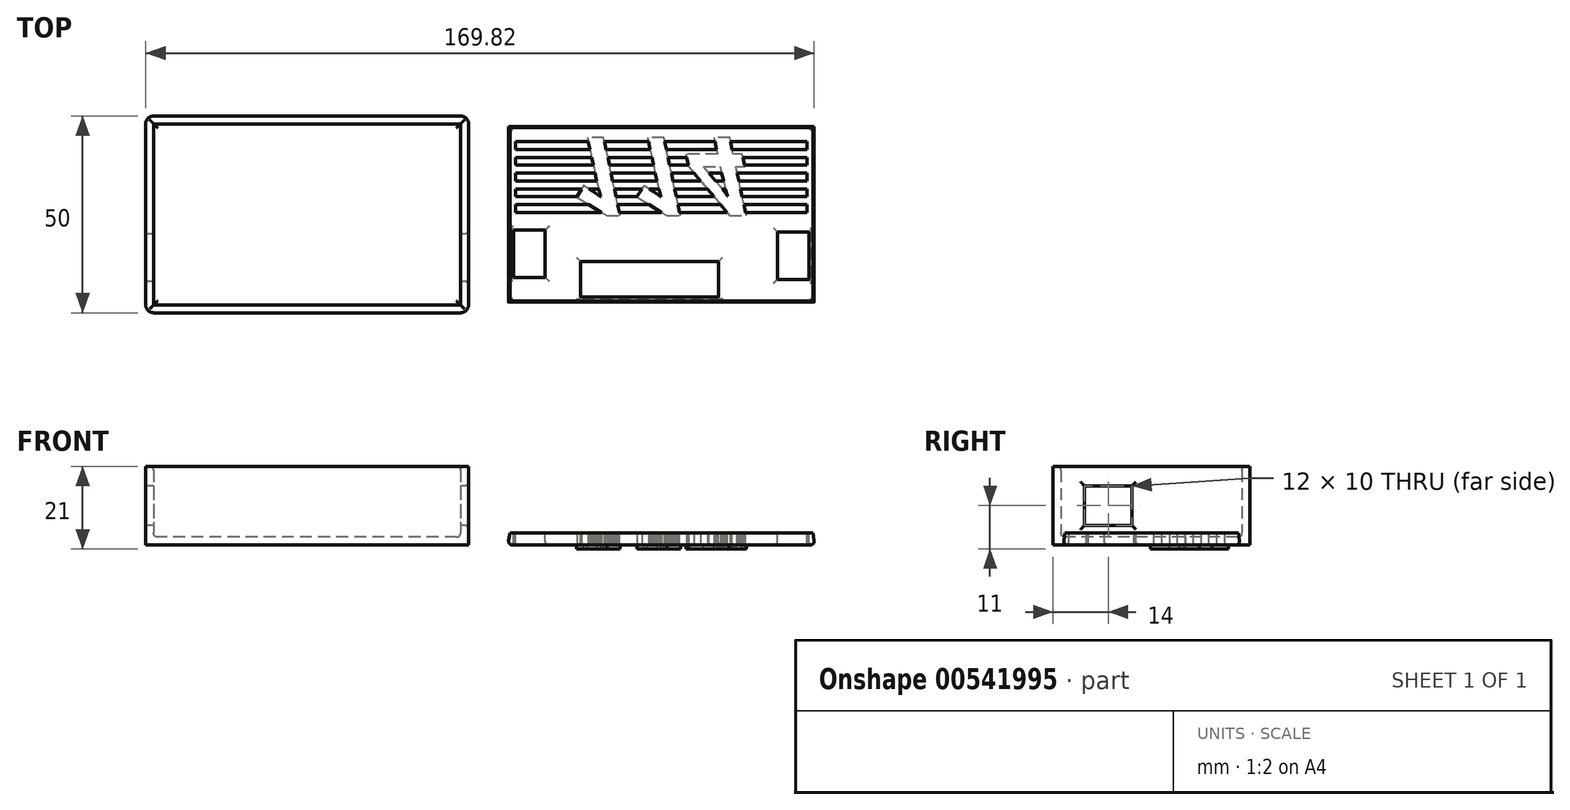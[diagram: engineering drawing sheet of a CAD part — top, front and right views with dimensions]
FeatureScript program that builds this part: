
annotation { "Feature Type Name" : "Feature", "Feature Type Description" : "" }
export const myFeature = defineFeature(function(context is Context, id is Id, definition is map)
    precondition{}
    {
        {
            var Q0;
            Q0=qCreatedBy(makeId("Top.planeOp"),FACE);
            var sketch = newSketch(context, id + "F0", { "sketchPlane" : qUnion([Q0])});
            skLineSegment(sketch, "E0.bottom", {"start": v(41, 25) * mm, "end": v(-41, 25) * mm});
            skLineSegment(sketch, "E0.top", {"start": v(41, -25) * mm, "end": v(-41, -25) * mm});
            skLineSegment(sketch, "E0.left", {"start": v(41, 25) * mm, "end": v(41, -25) * mm});
            skLineSegment(sketch, "E0.right", {"start": v(-41, 25) * mm, "end": v(-41, -25) * mm});
            skPoint(sketch, "E0.middle", {"position": v(0, 0) * mm});
            skSolve(sketch);
        }
        {
            var Q0;
            Q0 = qSketchRegion(id + "F0", true);
            extrude(context, id + "F1", {"entities" : qUnion([Q0]), "depth" : 20 * mm, "offsetDistance" : 25 * mm});
        }
        {
            var Q0;
            Q0=makeQuery(id+"F1.opExtrude","CAP_FACE",FACE,{"disambiguationData":[OSD([sQuery(id+"F0.wireOp",EDGE,"E0.bottom"),sQuery(id+"F0.wireOp",EDGE,"E0.top"),sQuery(id+"F0.wireOp",EDGE,"E0.left"),sQuery(id+"F0.wireOp",EDGE,"E0.right")])],"isStart":false});
            shell(context, id + "F2", {"entities" : qUnion([Q0]), "thickness" : 2 * mm});
        }
        {
            var Q0;
            Q0=makeQuery(id+"F1.opExtrude","SWEPT_EDGE",EDGE,{"disambiguationData":[OSD([sQuery(id+"F0.wireOp",EDGE,"E0.top"),sQuery(id+"F0.wireOp",EDGE,"E0.left")])]});
            var Q1;
            Q1=makeQuery(id+"F1.opExtrude","SWEPT_EDGE",EDGE,{"disambiguationData":[OSD([sQuery(id+"F0.wireOp",EDGE,"E0.top"),sQuery(id+"F0.wireOp",EDGE,"E0.right")])]});
            var Q2;
            Q2=makeQuery(id+"F1.opExtrude","SWEPT_EDGE",EDGE,{"disambiguationData":[OSD([sQuery(id+"F0.wireOp",EDGE,"E0.bottom"),sQuery(id+"F0.wireOp",EDGE,"E0.left")])]});
            var Q3;
            Q3=makeQuery(id+"F1.opExtrude","SWEPT_EDGE",EDGE,{"disambiguationData":[OSD([sQuery(id+"F0.wireOp",EDGE,"E0.bottom"),sQuery(id+"F0.wireOp",EDGE,"E0.right")])]});
            fillet(context, id + "F3", {"entities" : qUnion([Q0, Q1, Q2, Q3]), "radius" : 2 * mm, "tangentPropagation" : true, "allowEdgeOverflow" : false});
        }
        {
            var Q0;
            {var subQ0=sQuery(id+"F0.wireOp",EDGE,"E0.right");Q0=makeQuery(id+"F2.opShell","OFFSET_EDGE",EDGE,{"disambiguationData":[OSD([subQ0]),TDD([makeQuery(id+"F1.opExtrude","CAP_EDGE",EDGE,{"disambiguationData":[OSD([subQ0])],"isStart":false})])]});}
            var Q1;
            {var subQ0=sQuery(id+"F0.wireOp",EDGE,"E0.top");Q1=makeQuery(id+"F2.opShell","OFFSET_EDGE",EDGE,{"disambiguationData":[OSD([subQ0]),TDD([makeQuery(id+"F1.opExtrude","CAP_EDGE",EDGE,{"disambiguationData":[OSD([subQ0])],"isStart":false})])]});}
            var Q2;
            {var subQ0=sQuery(id+"F0.wireOp",EDGE,"E0.left");Q2=makeQuery(id+"F2.opShell","OFFSET_EDGE",EDGE,{"disambiguationData":[OSD([subQ0]),TDD([makeQuery(id+"F1.opExtrude","CAP_EDGE",EDGE,{"disambiguationData":[OSD([subQ0])],"isStart":false})])]});}
            var Q3;
            {var subQ0=sQuery(id+"F0.wireOp",EDGE,"E0.bottom");Q3=makeQuery(id+"F2.opShell","OFFSET_EDGE",EDGE,{"disambiguationData":[OSD([subQ0]),TDD([makeQuery(id+"F1.opExtrude","CAP_EDGE",EDGE,{"disambiguationData":[OSD([subQ0])],"isStart":true})])]});}
            var Q4;
            {var subQ0=sQuery(id+"F0.wireOp",EDGE,"E0.top");Q4=makeQuery(id+"F2.opShell","OFFSET_EDGE",EDGE,{"disambiguationData":[OSD([subQ0]),TDD([makeQuery(id+"F1.opExtrude","CAP_EDGE",EDGE,{"disambiguationData":[OSD([subQ0])],"isStart":true})])]});}
            var Q5;
            {var subQ0=sQuery(id+"F0.wireOp",EDGE,"E0.right");Q5=makeQuery(id+"F2.opShell","OFFSET_EDGE",EDGE,{"disambiguationData":[OSD([subQ0]),TDD([makeQuery(id+"F1.opExtrude","CAP_EDGE",EDGE,{"disambiguationData":[OSD([subQ0])],"isStart":true})])]});}
            var Q6;
            {var subQ0=sQuery(id+"F0.wireOp",EDGE,"E0.left");Q6=makeQuery(id+"F2.opShell","OFFSET_EDGE",EDGE,{"disambiguationData":[OSD([subQ0]),TDD([makeQuery(id+"F1.opExtrude","CAP_EDGE",EDGE,{"disambiguationData":[OSD([subQ0])],"isStart":true})])]});}
            var Q7;
            {var subQ0=sQuery(id+"F0.wireOp",EDGE,"E0.bottom");Q7=makeQuery(id+"F2.opShell","OFFSET_EDGE",EDGE,{"disambiguationData":[OSD([subQ0]),TDD([makeQuery(id+"F1.opExtrude","CAP_EDGE",EDGE,{"disambiguationData":[OSD([subQ0])],"isStart":false})])]});}
            fillet(context, id + "F4", {"entities" : qUnion([Q0, Q1, Q2, Q3, Q4, Q5, Q6, Q7]), "radius" : 1 * mm, "tangentPropagation" : true, "allowEdgeOverflow" : false});
        }
        {
            var Q0;
            Q0=qCreatedBy(makeId("Top.planeOp"),FACE);
            var sketch = newSketch(context, id + "F5", { "sketchPlane" : qUnion([Q0])});
            skLineSegment(sketch, "E1.bottom", {"start": v(129, 22.5) * mm, "end": v(51, 22.5) * mm});
            skLineSegment(sketch, "E1.top", {"start": v(129, -22.5) * mm, "end": v(51, -22.5) * mm});
            skLineSegment(sketch, "E1.left", {"start": v(129, 22.5) * mm, "end": v(129, -22.5) * mm});
            skLineSegment(sketch, "E1.right", {"start": v(51, 22.5) * mm, "end": v(51, -22.5) * mm});
            skPoint(sketch, "E1.middle", {"position": v(90, 0) * mm});
            skSolve(sketch);
        }
        {
            var Q0;
            Q0 = qSketchRegion(id + "F5", true);
            extrude(context, id + "F6", {"entities" : qUnion([Q0]), "depth" : 3 * mm, "offsetDistance" : 25 * mm});
        }
        {
            var Q0;
            Q0=makeQuery(id+"F6.opExtrude","CAP_FACE",FACE,{"disambiguationData":[OSD([sQuery(id+"F5.wireOp",EDGE,"E1.bottom"),sQuery(id+"F5.wireOp",EDGE,"E1.top"),sQuery(id+"F5.wireOp",EDGE,"E1.left"),sQuery(id+"F5.wireOp",EDGE,"E1.right")])],"isStart":false});
            shell(context, id + "F7", {"entities" : qUnion([Q0]), "thickness" : 2 * mm});
        }
        {
            var Q0;
            Q0=makeQuery(id+"F6.opExtrude","CAP_EDGE",EDGE,{"disambiguationData":[OSD([sQuery(id+"F5.wireOp",EDGE,"E1.top")])],"isStart":false});
            var Q1;
            Q1=makeQuery(id+"F6.opExtrude","CAP_EDGE",EDGE,{"disambiguationData":[OSD([sQuery(id+"F5.wireOp",EDGE,"E1.left")])],"isStart":false});
            var Q2;
            Q2=makeQuery(id+"F6.opExtrude","CAP_EDGE",EDGE,{"disambiguationData":[OSD([sQuery(id+"F5.wireOp",EDGE,"E1.bottom")])],"isStart":false});
            var Q3;
            Q3=makeQuery(id+"F6.opExtrude","CAP_EDGE",EDGE,{"disambiguationData":[OSD([sQuery(id+"F5.wireOp",EDGE,"E1.right")])],"isStart":false});
            chamfer(context, id + "F8", {"entities" : qUnion([Q0, Q1, Q2, Q3]), "chamferType" : ChamferType.TWO_OFFSETS, "width1" : 3 * mm, "oppositeDirection" : false, "width2" : .5 * mm, "tangentPropagation" : true});
        }
        {
            var Q0;
            Q0=makeQuery(id+"F7.opShell","OFFSET_FACE",FACE,{"disambiguationData":[OSD([sQuery(id+"F5.wireOp",EDGE,"E1.bottom"),sQuery(id+"F5.wireOp",EDGE,"E1.top"),sQuery(id+"F5.wireOp",EDGE,"E1.left"),sQuery(id+"F5.wireOp",EDGE,"E1.right")])]});
            var sketch = newSketch(context, id + "F9", { "sketchPlane" : qUnion([Q0])});
            skLineSegment(sketch, "E2.bottom", {"start": v(52.5, -16) * mm, "end": v(60.5, -16) * mm});
            skLineSegment(sketch, "E2.top", {"start": v(52.5, -4) * mm, "end": v(60.5, -4) * mm});
            skLineSegment(sketch, "E2.left", {"start": v(52.5, -16) * mm, "end": v(52.5, -4) * mm});
            skLineSegment(sketch, "E2.right", {"start": v(60.5, -16) * mm, "end": v(60.5, -4) * mm});
            skLineSegment(sketch, "E3.bottom", {"start": v(119.5, -16.5) * mm, "end": v(127.5, -16.5) * mm});
            skLineSegment(sketch, "E3.top", {"start": v(119.5, -4.5) * mm, "end": v(127.5, -4.5) * mm});
            skLineSegment(sketch, "E3.left", {"start": v(119.5, -16.5) * mm, "end": v(119.5, -4.5) * mm});
            skLineSegment(sketch, "E3.right", {"start": v(127.5, -16.5) * mm, "end": v(127.5, -4.5) * mm});
            skSolve(sketch);
        }
        {
            var Q0;
            Q0 = qSketchRegion(id + "F9", true);
            extrude(context, id + "F10", {"entities" : qUnion([Q0]), "operationType" : NewBodyOperationType.REMOVE, "oppositeDirection" : true, "depth" : 25 * mm, "offsetDistance" : 25 * mm, "symmetric" : true});
        }
        {
            var Q0;
            Q0=makeQuery(id+"F1.opExtrude","SWEPT_FACE",FACE,{"disambiguationData":[OSD([sQuery(id+"F0.wireOp",EDGE,"E0.right")])]});
            var sketch = newSketch(context, id + "F11", { "sketchPlane" : qUnion([Q0])});
            skLineSegment(sketch, "E4.bottom", {"start": v(5, 5) * mm, "end": v(17, 5) * mm});
            skLineSegment(sketch, "E4.top", {"start": v(5, 15) * mm, "end": v(17, 15) * mm});
            skLineSegment(sketch, "E4.left", {"start": v(5, 5) * mm, "end": v(5, 15) * mm});
            skLineSegment(sketch, "E4.right", {"start": v(17, 5) * mm, "end": v(17, 15) * mm});
            skSolve(sketch);
        }
        {
            var Q0;
            Q0 = qSketchRegion(id + "F11", true);
            extrude(context, id + "F12", {"entities" : qUnion([Q0]), "operationType" : NewBodyOperationType.REMOVE, "oppositeDirection" : true, "depth" : 90 * mm, "offsetDistance" : 25 * mm});
        }
        {
            var Q0;
            Q0=makeQuery(id+"F12.boolean.opBoolean","COPY",EDGE,{"derivedFrom":makeQuery(id+"F12.opExtrude","CAP_EDGE",EDGE,{"disambiguationData":[OSD([sQuery(id+"F11.wireOp",EDGE,"E4.left")])],"isStart":true})});
            var Q1;
            Q1=makeQuery(id+"F12.boolean.opBoolean","COPY",EDGE,{"derivedFrom":makeQuery(id+"F12.opExtrude","CAP_EDGE",EDGE,{"disambiguationData":[OSD([sQuery(id+"F11.wireOp",EDGE,"E4.top")])],"isStart":true})});
            var Q2;
            Q2=makeQuery(id+"F12.boolean.opBoolean","COPY",EDGE,{"derivedFrom":makeQuery(id+"F12.opExtrude","CAP_EDGE",EDGE,{"disambiguationData":[OSD([sQuery(id+"F11.wireOp",EDGE,"E4.right")])],"isStart":true})});
            var Q3;
            Q3=makeQuery(id+"F12.boolean.opBoolean","COPY",EDGE,{"derivedFrom":makeQuery(id+"F12.opExtrude","CAP_EDGE",EDGE,{"disambiguationData":[OSD([sQuery(id+"F11.wireOp",EDGE,"E4.bottom")])],"isStart":true})});
            var Q4;
            Q4=makeQuery(id+"F12.boolean.opBoolean","INTERSECT",EDGE,{"derivedFrom":[makeQuery(id+"F1.opExtrude","SWEPT_FACE",FACE,{"disambiguationData":[OSD([sQuery(id+"F0.wireOp",EDGE,"E0.left")])]}),makeQuery(id+"F12.opExtrude","SWEPT_FACE",FACE,{"disambiguationData":[OSD([sQuery(id+"F11.wireOp",EDGE,"E4.right")])]})]});
            var Q5;
            Q5=makeQuery(id+"F12.boolean.opBoolean","INTERSECT",EDGE,{"derivedFrom":[makeQuery(id+"F1.opExtrude","SWEPT_FACE",FACE,{"disambiguationData":[OSD([sQuery(id+"F0.wireOp",EDGE,"E0.left")])]}),makeQuery(id+"F12.opExtrude","SWEPT_FACE",FACE,{"disambiguationData":[OSD([sQuery(id+"F11.wireOp",EDGE,"E4.top")])]})]});
            var Q6;
            Q6=makeQuery(id+"F12.boolean.opBoolean","INTERSECT",EDGE,{"derivedFrom":[makeQuery(id+"F1.opExtrude","SWEPT_FACE",FACE,{"disambiguationData":[OSD([sQuery(id+"F0.wireOp",EDGE,"E0.left")])]}),makeQuery(id+"F12.opExtrude","SWEPT_FACE",FACE,{"disambiguationData":[OSD([sQuery(id+"F11.wireOp",EDGE,"E4.left")])]})]});
            var Q7;
            Q7=makeQuery(id+"F12.boolean.opBoolean","INTERSECT",EDGE,{"derivedFrom":[makeQuery(id+"F1.opExtrude","SWEPT_FACE",FACE,{"disambiguationData":[OSD([sQuery(id+"F0.wireOp",EDGE,"E0.left")])]}),makeQuery(id+"F12.opExtrude","SWEPT_FACE",FACE,{"disambiguationData":[OSD([sQuery(id+"F11.wireOp",EDGE,"E4.bottom")])]})]});
            fillet(context, id + "F13", {"entities" : qUnion([Q0, Q1, Q2, Q3, Q4, Q5, Q6, Q7]), "radius" : 1 * mm, "tangentPropagation" : true, "allowEdgeOverflow" : false});
        }
        {
            var Q0;
            Q0=makeQuery(id+"F7.opShell","OFFSET_FACE",FACE,{"disambiguationData":[OSD([sQuery(id+"F5.wireOp",EDGE,"E1.bottom"),sQuery(id+"F5.wireOp",EDGE,"E1.top"),sQuery(id+"F5.wireOp",EDGE,"E1.left"),sQuery(id+"F5.wireOp",EDGE,"E1.right")])]});
            var sketch = newSketch(context, id + "F14", { "sketchPlane" : qUnion([Q0])});
            skLineSegment(sketch, "E5.bottom", {"start": v(69.5, -21) * mm, "end": v(104.5, -21) * mm});
            skLineSegment(sketch, "E5.top", {"start": v(69.5, -12) * mm, "end": v(104.5, -12) * mm});
            skLineSegment(sketch, "E5.left", {"start": v(69.5, -21) * mm, "end": v(69.5, -12) * mm});
            skLineSegment(sketch, "E5.right", {"start": v(104.5, -21) * mm, "end": v(104.5, -12) * mm});
            skSolve(sketch);
        }
        {
            var Q0;
            Q0 = qSketchRegion(id + "F14", true);
            extrude(context, id + "F15", {"entities" : qUnion([Q0]), "operationType" : NewBodyOperationType.REMOVE, "oppositeDirection" : true, "depth" : 25 * mm, "offsetDistance" : 25 * mm, "symmetric" : true});
        }
        {
            var Q0;
            Q0=makeQuery(id+"F7.opShell","OFFSET_FACE",FACE,{"disambiguationData":[OSD([sQuery(id+"F5.wireOp",EDGE,"E1.bottom"),sQuery(id+"F5.wireOp",EDGE,"E1.top"),sQuery(id+"F5.wireOp",EDGE,"E1.left"),sQuery(id+"F5.wireOp",EDGE,"E1.right")])]});
            var sketch = newSketch(context, id + "F16", { "sketchPlane" : qUnion([Q0])});
            skLineSegment(sketch, "E6.bottom", {"start": v(53, 16.5) * mm, "end": v(127, 16.5) * mm});
            skLineSegment(sketch, "E6.top", {"start": v(53, 18.5) * mm, "end": v(127, 18.5) * mm});
            skLineSegment(sketch, "E6.left", {"start": v(53, 16.5) * mm, "end": v(53, 18.5) * mm});
            skLineSegment(sketch, "E6.right", {"start": v(127, 16.5) * mm, "end": v(127, 18.5) * mm});
            skLineSegment(sketch, "E7.bottom", {"start": v(53, 12.5) * mm, "end": v(127, 12.5) * mm});
            skLineSegment(sketch, "E7.top", {"start": v(53, 14.5) * mm, "end": v(127, 14.5) * mm});
            skLineSegment(sketch, "E7.left", {"start": v(53, 12.5) * mm, "end": v(53, 14.5) * mm});
            skLineSegment(sketch, "E7.right", {"start": v(127, 12.5) * mm, "end": v(127, 14.5) * mm});
            skLineSegment(sketch, "E8.bottom", {"start": v(53, 8.5) * mm, "end": v(127, 8.5) * mm});
            skLineSegment(sketch, "E8.top", {"start": v(53, 10.5) * mm, "end": v(127, 10.5) * mm});
            skLineSegment(sketch, "E8.left", {"start": v(53, 8.5) * mm, "end": v(53, 10.5) * mm});
            skLineSegment(sketch, "E8.right", {"start": v(127, 8.5) * mm, "end": v(127, 10.5) * mm});
            skLineSegment(sketch, "E9.bottom", {"start": v(53, 4.5) * mm, "end": v(127, 4.5) * mm});
            skLineSegment(sketch, "E9.top", {"start": v(53, 6.5) * mm, "end": v(127, 6.5) * mm});
            skLineSegment(sketch, "E9.left", {"start": v(53, 4.5) * mm, "end": v(53, 6.5) * mm});
            skLineSegment(sketch, "E9.right", {"start": v(127, 4.5) * mm, "end": v(127, 6.5) * mm});
            skLineSegment(sketch, "E10.bottom", {"start": v(53, 0.5) * mm, "end": v(127, 0.5) * mm});
            skLineSegment(sketch, "E10.top", {"start": v(53, 2.5) * mm, "end": v(127, 2.5) * mm});
            skLineSegment(sketch, "E10.left", {"start": v(53, 0.5) * mm, "end": v(53, 2.5) * mm});
            skLineSegment(sketch, "E10.right", {"start": v(127, 0.5) * mm, "end": v(127, 2.5) * mm});
            skSolve(sketch);
        }
        {
            var Q0;
            Q0 = qSketchRegion(id + "F16", true);
            extrude(context, id + "F17", {"entities" : qUnion([Q0]), "operationType" : NewBodyOperationType.REMOVE, "oppositeDirection" : true, "depth" : 25 * mm, "offsetDistance" : 25 * mm});
        }
        {
            var Q0;
            Q0=makeQuery(id+"F6.opExtrude","CAP_FACE",FACE,{"disambiguationData":[OSD([sQuery(id+"F5.wireOp",EDGE,"E1.bottom"),sQuery(id+"F5.wireOp",EDGE,"E1.top"),sQuery(id+"F5.wireOp",EDGE,"E1.left"),sQuery(id+"F5.wireOp",EDGE,"E1.right")])],"isStart":true});
            var sketch = newSketch(context, id + "F18", { "sketchPlane" : qUnion([Q0])});
            skText(sketch, "E11", { "text": "114", "fontName": "OpenSans-BoldItalic.ttf"});
            const initialGuessF18  = {"E11": [0.066, -0.0195, 1, 0, 0.02]};
            skSetInitialGuess(sketch, initialGuessF18);
            skSolve(sketch);
        }
        {
            var Q0;
            Q0 = qSketchRegion(id + "F18", true);
            extrude(context, id + "F19", {"entities" : qUnion([Q0]), "operationType" : NewBodyOperationType.ADD, "depth" : 4 * mm, "offsetDistance" : 25 * mm, "symmetric" : true});
        }
        {
            var Q0;
            {var subQ4=sQuery(id+"F5.wireOp",EDGE,"E1.left");var subQ9=sQuery(id+"F5.wireOp",EDGE,"E1.right");var subQ14=sQuery(id+"F5.wireOp",EDGE,"E1.top");var subQ15=sQuery(id+"F5.wireOp",EDGE,"E1.bottom");var subQ16=makeQuery(id+"F7.opShell","OFFSET_FACE",FACE,{"disambiguationData":[OSD([subQ15,subQ14,subQ4,subQ9])]});Q0=makeQuery(id+"F19.boolean.opBoolean","MERGE",FACE,{"derivedFrom":[makeQuery(id+"F17.boolean.opBoolean","SPLIT",FACE,{"disambiguationData":[TD([makeQuery(id+"F7.opShell","OFFSET_FACE",FACE,{"disambiguationData":[OSD([subQ15])]})])],"derivedFrom":subQ16}),makeQuery(id+"F17.boolean.opBoolean","SPLIT",FACE,{"disambiguationData":[TD([makeQuery(id+"F7.opShell","OFFSET_FACE",FACE,{"disambiguationData":[OSD([subQ14])]})])],"derivedFrom":subQ16}),makeQuery(id+"F17.boolean.opBoolean","SPLIT",FACE,{"disambiguationData":[TD([makeQuery(id+"F17.opExtrude","SWEPT_FACE",FACE,{"disambiguationData":[OSD([sQuery(id+"F16.wireOp",EDGE,"E6.bottom")])]})])],"derivedFrom":subQ16}),makeQuery(id+"F17.boolean.opBoolean","SPLIT",FACE,{"disambiguationData":[TD([makeQuery(id+"F17.opExtrude","SWEPT_FACE",FACE,{"disambiguationData":[OSD([sQuery(id+"F16.wireOp",EDGE,"E7.bottom")])]})])],"derivedFrom":subQ16}),makeQuery(id+"F17.boolean.opBoolean","SPLIT",FACE,{"disambiguationData":[TD([makeQuery(id+"F17.opExtrude","SWEPT_FACE",FACE,{"disambiguationData":[OSD([sQuery(id+"F16.wireOp",EDGE,"E8.bottom")])]})])],"derivedFrom":subQ16}),makeQuery(id+"F17.boolean.opBoolean","SPLIT",FACE,{"disambiguationData":[TD([makeQuery(id+"F17.opExtrude","SWEPT_FACE",FACE,{"disambiguationData":[OSD([sQuery(id+"F16.wireOp",EDGE,"E9.bottom")])]})])],"derivedFrom":subQ16}),makeQuery(id+"F19.opExtrude","CAP_FACE",FACE,{"disambiguationData":[OSD([sQuery(id+"F18.wireOp",EDGE,"E11.sketch_text.stroke-0"),sQuery(id+"F18.wireOp",EDGE,"E11.sketch_text.stroke-1"),sQuery(id+"F18.wireOp",EDGE,"E11.sketch_text.stroke-2"),sQuery(id+"F18.wireOp",EDGE,"E11.sketch_text.stroke-3"),sQuery(id+"F18.wireOp",EDGE,"E11.sketch_text.stroke-4"),sQuery(id+"F18.wireOp",EDGE,"E11.sketch_text.stroke-5"),sQuery(id+"F18.wireOp",EDGE,"E11.sketch_text.stroke-6"),sQuery(id+"F18.wireOp",EDGE,"E11.sketch_text.stroke-7"),sQuery(id+"F18.wireOp",EDGE,"E11.sketch_text.stroke-8")])],"isStart":true}),makeQuery(id+"F19.opExtrude","CAP_FACE",FACE,{"disambiguationData":[OSD([sQuery(id+"F18.wireOp",EDGE,"E11.sketch_text.stroke-9"),sQuery(id+"F18.wireOp",EDGE,"E11.sketch_text.stroke-10"),sQuery(id+"F18.wireOp",EDGE,"E11.sketch_text.stroke-11"),sQuery(id+"F18.wireOp",EDGE,"E11.sketch_text.stroke-12"),sQuery(id+"F18.wireOp",EDGE,"E11.sketch_text.stroke-13"),sQuery(id+"F18.wireOp",EDGE,"E11.sketch_text.stroke-14"),sQuery(id+"F18.wireOp",EDGE,"E11.sketch_text.stroke-15"),sQuery(id+"F18.wireOp",EDGE,"E11.sketch_text.stroke-16"),sQuery(id+"F18.wireOp",EDGE,"E11.sketch_text.stroke-17")])],"isStart":true}),makeQuery(id+"F19.opExtrude","CAP_FACE",FACE,{"disambiguationData":[OSD([sQuery(id+"F18.wireOp",EDGE,"E11.sketch_text.stroke-18"),sQuery(id+"F18.wireOp",EDGE,"E11.sketch_text.stroke-19"),sQuery(id+"F18.wireOp",EDGE,"E11.sketch_text.stroke-20"),sQuery(id+"F18.wireOp",EDGE,"E11.sketch_text.stroke-21"),sQuery(id+"F18.wireOp",EDGE,"E11.sketch_text.stroke-22"),sQuery(id+"F18.wireOp",EDGE,"E11.sketch_text.stroke-23"),sQuery(id+"F18.wireOp",EDGE,"E11.sketch_text.stroke-24"),sQuery(id+"F18.wireOp",EDGE,"E11.sketch_text.stroke-25"),sQuery(id+"F18.wireOp",EDGE,"E11.sketch_text.stroke-26"),sQuery(id+"F18.wireOp",EDGE,"E11.sketch_text.stroke-27"),sQuery(id+"F18.wireOp",EDGE,"E11.sketch_text.stroke-28"),sQuery(id+"F18.wireOp",EDGE,"E11.sketch_text.stroke-29"),sQuery(id+"F18.wireOp",EDGE,"E11.sketch_text.stroke-30"),sQuery(id+"F18.wireOp",EDGE,"E11.sketch_text.stroke-31"),sQuery(id+"F18.wireOp",EDGE,"E11.sketch_text.stroke-32"),sQuery(id+"F18.wireOp",EDGE,"E11.sketch_text.stroke-33"),sQuery(id+"F18.wireOp",EDGE,"E11.sketch_text.stroke-34"),sQuery(id+"F18.wireOp",EDGE,"E11.sketch_text.stroke-35")])],"isStart":true})]});}
            extrude(context, id + "F20", {"entities" : qUnion([Q0]), "operationType" : NewBodyOperationType.ADD, "depth" : 1 * mm, "offsetDistance" : 25 * mm});
        }
        {
            var Q0;
            Q0=makeQuery(id+"F19.opExtrude","CAP_FACE",FACE,{"disambiguationData":[OSD([sQuery(id+"F18.wireOp",EDGE,"E11.sketch_text.stroke-0"),sQuery(id+"F18.wireOp",EDGE,"E11.sketch_text.stroke-1"),sQuery(id+"F18.wireOp",EDGE,"E11.sketch_text.stroke-2"),sQuery(id+"F18.wireOp",EDGE,"E11.sketch_text.stroke-3"),sQuery(id+"F18.wireOp",EDGE,"E11.sketch_text.stroke-4"),sQuery(id+"F18.wireOp",EDGE,"E11.sketch_text.stroke-5"),sQuery(id+"F18.wireOp",EDGE,"E11.sketch_text.stroke-6"),sQuery(id+"F18.wireOp",EDGE,"E11.sketch_text.stroke-7"),sQuery(id+"F18.wireOp",EDGE,"E11.sketch_text.stroke-8")])],"isStart":false});
            var Q1;
            Q1=makeQuery(id+"F19.opExtrude","CAP_FACE",FACE,{"disambiguationData":[OSD([sQuery(id+"F18.wireOp",EDGE,"E11.sketch_text.stroke-9"),sQuery(id+"F18.wireOp",EDGE,"E11.sketch_text.stroke-10"),sQuery(id+"F18.wireOp",EDGE,"E11.sketch_text.stroke-11"),sQuery(id+"F18.wireOp",EDGE,"E11.sketch_text.stroke-12"),sQuery(id+"F18.wireOp",EDGE,"E11.sketch_text.stroke-13"),sQuery(id+"F18.wireOp",EDGE,"E11.sketch_text.stroke-14"),sQuery(id+"F18.wireOp",EDGE,"E11.sketch_text.stroke-15"),sQuery(id+"F18.wireOp",EDGE,"E11.sketch_text.stroke-16"),sQuery(id+"F18.wireOp",EDGE,"E11.sketch_text.stroke-17")])],"isStart":false});
            var Q2;
            Q2=makeQuery(id+"F19.opExtrude","CAP_FACE",FACE,{"disambiguationData":[OSD([sQuery(id+"F18.wireOp",EDGE,"E11.sketch_text.stroke-18"),sQuery(id+"F18.wireOp",EDGE,"E11.sketch_text.stroke-19"),sQuery(id+"F18.wireOp",EDGE,"E11.sketch_text.stroke-20"),sQuery(id+"F18.wireOp",EDGE,"E11.sketch_text.stroke-21"),sQuery(id+"F18.wireOp",EDGE,"E11.sketch_text.stroke-22"),sQuery(id+"F18.wireOp",EDGE,"E11.sketch_text.stroke-23"),sQuery(id+"F18.wireOp",EDGE,"E11.sketch_text.stroke-24"),sQuery(id+"F18.wireOp",EDGE,"E11.sketch_text.stroke-25"),sQuery(id+"F18.wireOp",EDGE,"E11.sketch_text.stroke-26"),sQuery(id+"F18.wireOp",EDGE,"E11.sketch_text.stroke-27"),sQuery(id+"F18.wireOp",EDGE,"E11.sketch_text.stroke-28"),sQuery(id+"F18.wireOp",EDGE,"E11.sketch_text.stroke-29"),sQuery(id+"F18.wireOp",EDGE,"E11.sketch_text.stroke-30"),sQuery(id+"F18.wireOp",EDGE,"E11.sketch_text.stroke-31"),sQuery(id+"F18.wireOp",EDGE,"E11.sketch_text.stroke-32"),sQuery(id+"F18.wireOp",EDGE,"E11.sketch_text.stroke-33"),sQuery(id+"F18.wireOp",EDGE,"E11.sketch_text.stroke-34"),sQuery(id+"F18.wireOp",EDGE,"E11.sketch_text.stroke-35")])],"isStart":false});
            extrude(context, id + "F21", {"entities" : qUnion([Q0, Q1, Q2]), "operationType" : NewBodyOperationType.REMOVE, "oppositeDirection" : true, "depth" : 1 * mm, "offsetDistance" : 25 * mm});
        }
        {
            var Q0;
            Q0=makeQuery(id+"F10.boolean.opBoolean","INTERSECT",EDGE,{"derivedFrom":[makeQuery(id+"F6.opExtrude","CAP_FACE",FACE,{"disambiguationData":[OSD([sQuery(id+"F5.wireOp",EDGE,"E1.bottom"),sQuery(id+"F5.wireOp",EDGE,"E1.top"),sQuery(id+"F5.wireOp",EDGE,"E1.left"),sQuery(id+"F5.wireOp",EDGE,"E1.right")])],"isStart":true}),makeQuery(id+"F10.opExtrude","SWEPT_FACE",FACE,{"disambiguationData":[OSD([sQuery(id+"F9.wireOp",EDGE,"E2.bottom")])]})]});
            var Q1;
            Q1=makeQuery(id+"F10.boolean.opBoolean","INTERSECT",EDGE,{"derivedFrom":[makeQuery(id+"F6.opExtrude","CAP_FACE",FACE,{"disambiguationData":[OSD([sQuery(id+"F5.wireOp",EDGE,"E1.bottom"),sQuery(id+"F5.wireOp",EDGE,"E1.top"),sQuery(id+"F5.wireOp",EDGE,"E1.left"),sQuery(id+"F5.wireOp",EDGE,"E1.right")])],"isStart":true}),makeQuery(id+"F10.opExtrude","SWEPT_FACE",FACE,{"disambiguationData":[OSD([sQuery(id+"F9.wireOp",EDGE,"E2.left")])]})]});
            var Q2;
            Q2=makeQuery(id+"F10.boolean.opBoolean","INTERSECT",EDGE,{"derivedFrom":[makeQuery(id+"F6.opExtrude","CAP_FACE",FACE,{"disambiguationData":[OSD([sQuery(id+"F5.wireOp",EDGE,"E1.bottom"),sQuery(id+"F5.wireOp",EDGE,"E1.top"),sQuery(id+"F5.wireOp",EDGE,"E1.left"),sQuery(id+"F5.wireOp",EDGE,"E1.right")])],"isStart":true}),makeQuery(id+"F10.opExtrude","SWEPT_FACE",FACE,{"disambiguationData":[OSD([sQuery(id+"F9.wireOp",EDGE,"E2.right")])]})]});
            var Q3;
            Q3=makeQuery(id+"F10.boolean.opBoolean","INTERSECT",EDGE,{"derivedFrom":[makeQuery(id+"F6.opExtrude","CAP_FACE",FACE,{"disambiguationData":[OSD([sQuery(id+"F5.wireOp",EDGE,"E1.bottom"),sQuery(id+"F5.wireOp",EDGE,"E1.top"),sQuery(id+"F5.wireOp",EDGE,"E1.left"),sQuery(id+"F5.wireOp",EDGE,"E1.right")])],"isStart":true}),makeQuery(id+"F10.opExtrude","SWEPT_FACE",FACE,{"disambiguationData":[OSD([sQuery(id+"F9.wireOp",EDGE,"E2.top")])]})]});
            var Q4;
            Q4=makeQuery(id+"F10.boolean.opBoolean","INTERSECT",EDGE,{"derivedFrom":[makeQuery(id+"F6.opExtrude","CAP_FACE",FACE,{"disambiguationData":[OSD([sQuery(id+"F5.wireOp",EDGE,"E1.bottom"),sQuery(id+"F5.wireOp",EDGE,"E1.top"),sQuery(id+"F5.wireOp",EDGE,"E1.left"),sQuery(id+"F5.wireOp",EDGE,"E1.right")])],"isStart":true}),makeQuery(id+"F10.opExtrude","SWEPT_FACE",FACE,{"disambiguationData":[OSD([sQuery(id+"F9.wireOp",EDGE,"E3.bottom")])]})]});
            var Q5;
            Q5=makeQuery(id+"F10.boolean.opBoolean","INTERSECT",EDGE,{"derivedFrom":[makeQuery(id+"F6.opExtrude","CAP_FACE",FACE,{"disambiguationData":[OSD([sQuery(id+"F5.wireOp",EDGE,"E1.bottom"),sQuery(id+"F5.wireOp",EDGE,"E1.top"),sQuery(id+"F5.wireOp",EDGE,"E1.left"),sQuery(id+"F5.wireOp",EDGE,"E1.right")])],"isStart":true}),makeQuery(id+"F10.opExtrude","SWEPT_FACE",FACE,{"disambiguationData":[OSD([sQuery(id+"F9.wireOp",EDGE,"E3.left")])]})]});
            var Q6;
            Q6=makeQuery(id+"F10.boolean.opBoolean","INTERSECT",EDGE,{"derivedFrom":[makeQuery(id+"F6.opExtrude","CAP_FACE",FACE,{"disambiguationData":[OSD([sQuery(id+"F5.wireOp",EDGE,"E1.bottom"),sQuery(id+"F5.wireOp",EDGE,"E1.top"),sQuery(id+"F5.wireOp",EDGE,"E1.left"),sQuery(id+"F5.wireOp",EDGE,"E1.right")])],"isStart":true}),makeQuery(id+"F10.opExtrude","SWEPT_FACE",FACE,{"disambiguationData":[OSD([sQuery(id+"F9.wireOp",EDGE,"E3.top")])]})]});
            var Q7;
            Q7=makeQuery(id+"F10.boolean.opBoolean","INTERSECT",EDGE,{"derivedFrom":[makeQuery(id+"F6.opExtrude","CAP_FACE",FACE,{"disambiguationData":[OSD([sQuery(id+"F5.wireOp",EDGE,"E1.bottom"),sQuery(id+"F5.wireOp",EDGE,"E1.top"),sQuery(id+"F5.wireOp",EDGE,"E1.left"),sQuery(id+"F5.wireOp",EDGE,"E1.right")])],"isStart":true}),makeQuery(id+"F10.opExtrude","SWEPT_FACE",FACE,{"disambiguationData":[OSD([sQuery(id+"F9.wireOp",EDGE,"E3.right")])]})]});
            var Q8;
            Q8=makeQuery(id+"F15.boolean.opBoolean","INTERSECT",EDGE,{"derivedFrom":[makeQuery(id+"F6.opExtrude","CAP_FACE",FACE,{"disambiguationData":[OSD([sQuery(id+"F5.wireOp",EDGE,"E1.bottom"),sQuery(id+"F5.wireOp",EDGE,"E1.top"),sQuery(id+"F5.wireOp",EDGE,"E1.left"),sQuery(id+"F5.wireOp",EDGE,"E1.right")])],"isStart":true}),makeQuery(id+"F15.opExtrude","SWEPT_FACE",FACE,{"disambiguationData":[OSD([sQuery(id+"F14.wireOp",EDGE,"E5.top")])]})]});
            var Q9;
            Q9=makeQuery(id+"F15.boolean.opBoolean","INTERSECT",EDGE,{"derivedFrom":[makeQuery(id+"F6.opExtrude","CAP_FACE",FACE,{"disambiguationData":[OSD([sQuery(id+"F5.wireOp",EDGE,"E1.bottom"),sQuery(id+"F5.wireOp",EDGE,"E1.top"),sQuery(id+"F5.wireOp",EDGE,"E1.left"),sQuery(id+"F5.wireOp",EDGE,"E1.right")])],"isStart":true}),makeQuery(id+"F15.opExtrude","SWEPT_FACE",FACE,{"disambiguationData":[OSD([sQuery(id+"F14.wireOp",EDGE,"E5.left")])]})]});
            var Q10;
            Q10=makeQuery(id+"F15.boolean.opBoolean","INTERSECT",EDGE,{"derivedFrom":[makeQuery(id+"F6.opExtrude","CAP_FACE",FACE,{"disambiguationData":[OSD([sQuery(id+"F5.wireOp",EDGE,"E1.bottom"),sQuery(id+"F5.wireOp",EDGE,"E1.top"),sQuery(id+"F5.wireOp",EDGE,"E1.left"),sQuery(id+"F5.wireOp",EDGE,"E1.right")])],"isStart":true}),makeQuery(id+"F15.opExtrude","SWEPT_FACE",FACE,{"disambiguationData":[OSD([sQuery(id+"F14.wireOp",EDGE,"E5.bottom")])]})]});
            var Q11;
            Q11=makeQuery(id+"F15.boolean.opBoolean","INTERSECT",EDGE,{"derivedFrom":[makeQuery(id+"F6.opExtrude","CAP_FACE",FACE,{"disambiguationData":[OSD([sQuery(id+"F5.wireOp",EDGE,"E1.bottom"),sQuery(id+"F5.wireOp",EDGE,"E1.top"),sQuery(id+"F5.wireOp",EDGE,"E1.left"),sQuery(id+"F5.wireOp",EDGE,"E1.right")])],"isStart":true}),makeQuery(id+"F15.opExtrude","SWEPT_FACE",FACE,{"disambiguationData":[OSD([sQuery(id+"F14.wireOp",EDGE,"E5.right")])]})]});
            fillet(context, id + "F22", {"entities" : qUnion([Q0, Q1, Q2, Q3, Q4, Q5, Q6, Q7, Q8, Q9, Q10, Q11]), "radius" : 1 * mm, "tangentPropagation" : true, "allowEdgeOverflow" : false});
        }
        {
            var Q0;
            {var subQ0=sQuery(id+"F5.wireOp",EDGE,"E1.top");Q0=makeQuery(id+"F8.opChamfer","BLEND_EDGE",EDGE,{"blendedFrom":[makeQuery(id+"F6.opExtrude","CAP_EDGE",EDGE,{"disambiguationData":[OSD([subQ0])],"isStart":false}),makeQuery(id+"F6.opExtrude","CAP_FACE",FACE,{"disambiguationData":[OSD([sQuery(id+"F5.wireOp",EDGE,"E1.bottom"),subQ0,sQuery(id+"F5.wireOp",EDGE,"E1.left"),sQuery(id+"F5.wireOp",EDGE,"E1.right")])],"isStart":true})],"blendedInto":[makeQuery(id+"F6.opExtrude","CAP_FACE",FACE,{"disambiguationData":[OSD([sQuery(id+"F5.wireOp",EDGE,"E1.bottom"),subQ0,sQuery(id+"F5.wireOp",EDGE,"E1.left"),sQuery(id+"F5.wireOp",EDGE,"E1.right")])],"isStart":true})]});}
            var Q1;
            {var subQ0=sQuery(id+"F5.wireOp",EDGE,"E1.left");Q1=makeQuery(id+"F8.opChamfer","BLEND_EDGE",EDGE,{"blendedFrom":[makeQuery(id+"F6.opExtrude","CAP_EDGE",EDGE,{"disambiguationData":[OSD([subQ0])],"isStart":false}),makeQuery(id+"F6.opExtrude","CAP_FACE",FACE,{"disambiguationData":[OSD([sQuery(id+"F5.wireOp",EDGE,"E1.bottom"),sQuery(id+"F5.wireOp",EDGE,"E1.top"),subQ0,sQuery(id+"F5.wireOp",EDGE,"E1.right")])],"isStart":true})],"blendedInto":[makeQuery(id+"F6.opExtrude","CAP_FACE",FACE,{"disambiguationData":[OSD([sQuery(id+"F5.wireOp",EDGE,"E1.bottom"),sQuery(id+"F5.wireOp",EDGE,"E1.top"),subQ0,sQuery(id+"F5.wireOp",EDGE,"E1.right")])],"isStart":true})]});}
            var Q2;
            {var subQ0=sQuery(id+"F5.wireOp",EDGE,"E1.bottom");Q2=makeQuery(id+"F8.opChamfer","BLEND_EDGE",EDGE,{"blendedFrom":[makeQuery(id+"F6.opExtrude","CAP_EDGE",EDGE,{"disambiguationData":[OSD([subQ0])],"isStart":false}),makeQuery(id+"F6.opExtrude","CAP_FACE",FACE,{"disambiguationData":[OSD([subQ0,sQuery(id+"F5.wireOp",EDGE,"E1.top"),sQuery(id+"F5.wireOp",EDGE,"E1.left"),sQuery(id+"F5.wireOp",EDGE,"E1.right")])],"isStart":true})],"blendedInto":[makeQuery(id+"F6.opExtrude","CAP_FACE",FACE,{"disambiguationData":[OSD([subQ0,sQuery(id+"F5.wireOp",EDGE,"E1.top"),sQuery(id+"F5.wireOp",EDGE,"E1.left"),sQuery(id+"F5.wireOp",EDGE,"E1.right")])],"isStart":true})]});}
            var Q3;
            {var subQ0=sQuery(id+"F5.wireOp",EDGE,"E1.right");Q3=makeQuery(id+"F8.opChamfer","BLEND_EDGE",EDGE,{"blendedFrom":[makeQuery(id+"F6.opExtrude","CAP_EDGE",EDGE,{"disambiguationData":[OSD([subQ0])],"isStart":false}),makeQuery(id+"F6.opExtrude","CAP_FACE",FACE,{"disambiguationData":[OSD([sQuery(id+"F5.wireOp",EDGE,"E1.bottom"),sQuery(id+"F5.wireOp",EDGE,"E1.top"),sQuery(id+"F5.wireOp",EDGE,"E1.left"),subQ0])],"isStart":true})],"blendedInto":[makeQuery(id+"F6.opExtrude","CAP_FACE",FACE,{"disambiguationData":[OSD([sQuery(id+"F5.wireOp",EDGE,"E1.bottom"),sQuery(id+"F5.wireOp",EDGE,"E1.top"),sQuery(id+"F5.wireOp",EDGE,"E1.left"),subQ0])],"isStart":true})]});}
            fillet(context, id + "F23", {"entities" : qUnion([Q0, Q1, Q2, Q3]), "radius" : 1 * mm, "tangentPropagation" : true, "allowEdgeOverflow" : false});
        }
    });
